# Revit family: Door-Hardware_Exit-Device_Hager_4500
name_source: partatom
category: Specialty Equipment
units: mm (PartAtom-declared; Revit-internal decimal feet)

## family parameters
Always vertical = No
Classification Number = 23.30.40.31
Cut with Voids When Loaded = No
Enable Cutting in Views = No
Maintain Annotation Orientation = No
Part Type = Normal
Room Calculation Point = No
Round Connector Dimension = Use Diameter
Shared = Yes
Work Plane-Based = Yes

## types (1)
- Door-Hardware_Exit-Device_Hager_4500
    Assembly Code = C1020410
    Bottom Rod = Yes
    Default Elevation = 0' - 0"
    Expected Lifespan (Years) = 0
    Keynote = 087100
    Maintenance Schedule (Months) = 0
    Manufacturer = Hager Companies
    Manufacturer Fax = 800-782-0149
    Manufacturer Website = http://www.hagerco.com
    Model = As Specified
    Operating Temperature Range = Interior - Exterior
    Product Data = http://www.arcat.com
    Revision = R1_2015-10
    Sales Information = http://www.hagerco.com
    Specification = http://www.arcat.com
    Standards Conformance = as Specified
    Top Rod = Yes
    URL = http://www.hagerco.com
    Warranty Duration (Years) = 0

## geometry (parser evidence)
native form markers: Blend x6, Sweep x2
no freeform markers — native parametric forms only
